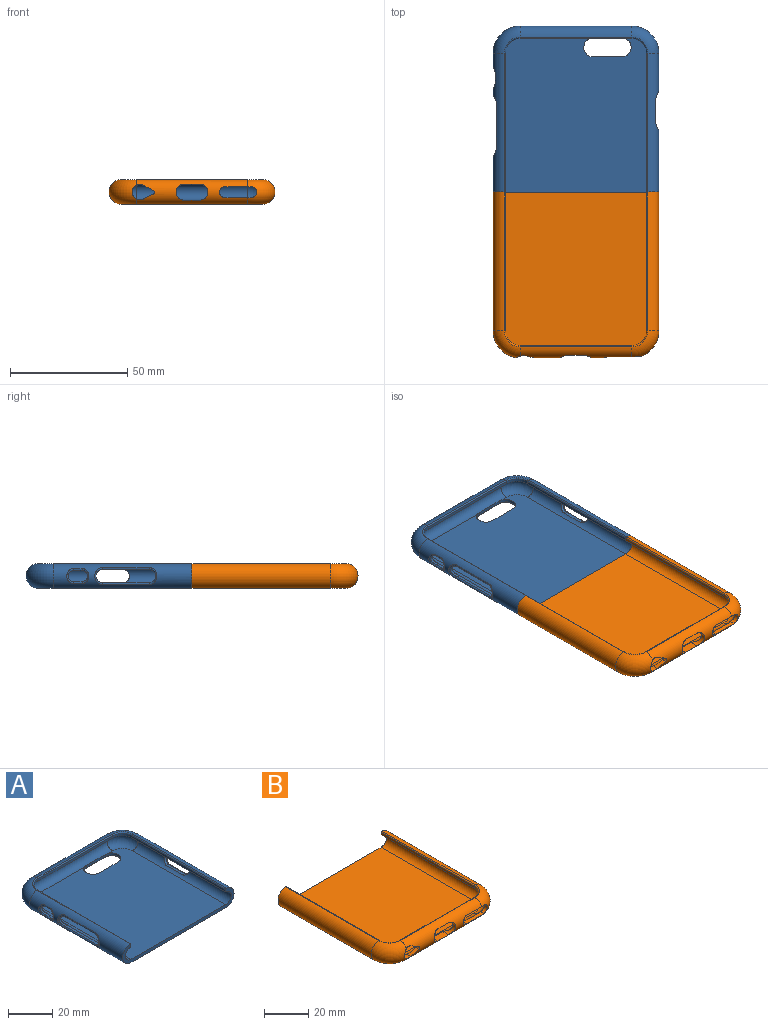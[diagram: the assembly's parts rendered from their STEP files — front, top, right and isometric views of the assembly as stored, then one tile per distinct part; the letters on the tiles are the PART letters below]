
ASSEMBLY  parts=2 mates=1
PART A: 57 faces, bbox 72.7x71.9x10.6 mm
  f0: plane 65.64x60.26mm, normal (0,0,1), area 3790.2mm2, adj f1,f3,f10,f11,f14,f19,f20,f21
  f1: cylinder r=3.5mm len=59.27mm, axis (0,-1,0), area 558.5mm2, adj f0,f2,f11,f40,f41,f42,f43,f56
  f2: plane 59.27x1.24mm, normal (-1,0,0), area 73.7mm2, adj f1,f8,f12,f56
  f3: cylinder r=3.5mm len=59.27mm, axis (0,1,0), area 456.4mm2, adj f0,f4,f14,f32,f33,f34,f35,f36
  f4: plane 59.27x1.24mm, normal (1,0,0), area 73.7mm2, adj f3,f9,f15,f56
  f5: cylinder r=5.28mm len=59.27mm, axis (0,-1,0), area 826.3mm2, adj f7,f8,f16,f44,f45,f46,f47,f56
  f6: cylinder r=5.28mm len=59.27mm, axis (0,1,0), area 691.2mm2, adj f7,f9,f18,f48,f49,f50,f51,f52
  f7: plane 65.64x60.26mm, normal (0,0,-1), area 3772.3mm2, adj f5,f6,f16,f17,f18,f23,f24,f25
  f8: cylinder r=0.51mm len=59.27mm, axis (0,-1,0), area 50.5mm2, adj f2,f5,f29,f56
  f9: cylinder r=0.51mm len=59.27mm, axis (0,1,0), area 50.5mm2, adj f4,f6,f31,f56
  f10: cylinder r=3.5mm len=47.52mm, axis (1,0,0), area 518.9mm2, adj f0,f11,f13,f14,f19,f21,f22
  f11: torus R=6.37mm, axis (0,0,-1), area 148.5mm2, adj f0,f1,f10,f12
  f12: cylinder r=6.37mm len=6.37mm, axis (0,0,-1), area 12.4mm2, adj f2,f11,f13,f29
  f13: plane 47.52x1.24mm, normal (0,-1,0), area 59.1mm2, adj f10,f12,f15,f30
  f14: torus R=6.37mm, axis (0,0,-1), area 148.5mm2, adj f0,f3,f10,f15
  f15: cylinder r=6.37mm len=6.37mm, axis (0,0,-1), area 12.4mm2, adj f4,f13,f14,f31
  f16: torus R=6.37mm, axis (0,0,-1), area 247.6mm2, adj f5,f7,f17,f29
  f17: cylinder r=5.28mm len=47.52mm, axis (1,0,0), area 748mm2, adj f7,f16,f18,f26,f27,f28,f30
  f18: torus R=6.37mm, axis (0,0,-1), area 247.6mm2, adj f6,f7,f17,f31
  f19: cylinder r=4.1mm len=8.2mm, axis (0,0,1), area 16.3mm2, adj f0,f10,f20,f22,f25,f27
  f20: plane 12.06x1.27mm, normal (0,1,0), area 15.3mm2, adj f0,f19,f21,f23
  f21: cylinder r=4.1mm len=8.2mm, axis (0,0,1), area 16.3mm2, adj f0,f10,f20,f22,f24,f26
  f22: plane 12.06x1.22mm, normal (0,-1,0), area 14.7mm2, adj f10,f19,f21,f28
  f23: cylinder r=0.51mm len=12.06mm, axis (1,0,0), area 9.6mm2, adj f7,f20,f24,f25
  f24: torus R=4.61mm, axis (0,0,-1), area 8.7mm2, adj f7,f21,f23,f26
  f25: torus R=4.61mm, axis (0,0,-1), area 8.7mm2, adj f7,f19,f23,f27
  f26: bspline ~4.26x1.79mm, area 2.1mm2, adj f17,f21,f24,f28
  f27: bspline ~4.26x1.79mm, area 2.1mm2, adj f17,f19,f25,f28
  f28: cylinder r=0.51mm len=12.06mm, axis (1,0,0), area 10.6mm2, adj f17,f22,f26,f27
  f29: torus R=6.88mm, axis (0,0,1), area 8.8mm2, adj f8,f12,f16,f30
  f30: cylinder r=0.51mm len=47.52mm, axis (1,0,0), area 40.5mm2, adj f13,f17,f29,f31
  f31: torus R=6.88mm, axis (0,0,1), area 8.8mm2, adj f9,f15,f18,f30
  f32: cylinder r=2.39mm len=4.77mm, axis (1,0,0), area 9.3mm2, adj f3,f33,f35,f55
  f33: plane 3.63x1.22mm, normal (0,0,-1), area 4.4mm2, adj f3,f32,f34,f53
  f34: cylinder r=2.39mm len=4.77mm, axis (1,0,0), area 9.3mm2, adj f3,f33,f35,f52
  f35: plane 3.63x1.24mm, normal (0,0,1), area 4.5mm2, adj f3,f32,f34,f54
  f36: cylinder r=2.8mm len=5.59mm, axis (1,0,0), area 11.3mm2, adj f3,f37,f39,f51
  f37: plane 20.01x1.32mm, normal (0,0,-1), area 26.4mm2, adj f3,f36,f38,f49
  f38: cylinder r=2.8mm len=5.59mm, axis (1,0,0), area 11.3mm2, adj f3,f37,f39,f48
  f39: plane 20.01x1.36mm, normal (0,0,1), area 27.1mm2, adj f3,f36,f38,f50
  f40: plane 10.2x1.32mm, normal (0,0,-1), area 13.4mm2, adj f1,f41,f43,f47
  f41: cylinder r=2.79mm len=5.59mm, axis (-1,0,0), area 11.3mm2, adj f1,f40,f42,f46
  f42: plane 10.2x1.35mm, normal (0,0,1), area 13.8mm2, adj f1,f41,f43,f44
  f43: cylinder r=2.79mm len=5.59mm, axis (-1,0,0), area 11.3mm2, adj f1,f40,f42,f45
  f44: cylinder r=0.51mm len=10.2mm, axis (0,-1,0), area 12.2mm2, adj f5,f42,f45,f46
  f45: bspline ~7.31x3.93mm, area 9.8mm2, adj f5,f43,f44,f47
  f46: bspline ~7.31x3.94mm, area 9.8mm2, adj f5,f41,f44,f47
  f47: cylinder r=0.51mm len=10.2mm, axis (0,-1,0), area 12mm2, adj f5,f40,f45,f46
  f48: bspline ~7.31x3.94mm, area 9.8mm2, adj f6,f38,f49,f50
  f49: cylinder r=0.51mm len=20.01mm, axis (0,1,0), area 23.6mm2, adj f6,f37,f48,f51
  f50: cylinder r=0.51mm len=20.01mm, axis (0,1,0), area 23.9mm2, adj f6,f39,f48,f51
  f51: bspline ~7.31x3.94mm, area 9.8mm2, adj f6,f36,f49,f50
  f52: bspline ~6.41x3.47mm, area 8.2mm2, adj f6,f34,f53,f54
  f53: cylinder r=0.51mm len=3.63mm, axis (0,1,0), area 4.1mm2, adj f6,f33,f52,f55
  f54: cylinder r=0.51mm len=3.63mm, axis (0,1,0), area 4.1mm2, adj f6,f35,f52,f55
  f55: bspline ~6.41x3.48mm, area 8.2mm2, adj f6,f32,f53,f54
  f56: plane 70.82x10.53mm, normal (0,-1,0), area 156mm2, adj f0,f1,f2,f3,f4,f5,f6,f7
PART B: 35 faces, bbox 72.7x71.9x10.5 mm
  f0: plane 47.52x1.24mm, normal (0,1,0), area 59.1mm2, adj f13,f14,f16,f18
  f1: cylinder r=2.32mm len=4.65mm, axis (0,1,0), area 14.2mm2, adj f10,f12,f14,f20
  f2: plane 4.25x3.4mm, normal (-0.43,0,0.9), area 9.7mm2, adj f3,f5,f14,f20
  f3: cylinder r=1mm len=1.92mm, axis (0,1,0), area 4mm2, adj f2,f4,f14,f20
  f4: plane 4.25x3.19mm, normal (-0.43,0,-0.9), area 9.5mm2, adj f3,f5,f14,f20
  f5: cylinder r=3.25mm len=6.5mm, axis (0,1,0), area 30.6mm2, adj f2,f4,f14,f17,f19,f20
  f6: plane 6.85x3.59mm, normal (0,0,1), area 24.6mm2, adj f7,f9,f14,f20
  f7: cylinder r=3.4mm len=6.8mm, axis (0,1,0), area 24.7mm2, adj f6,f8,f14,f20
  f8: plane 6.85x3mm, normal (0,0,-1), area 20.5mm2, adj f7,f9,f14,f20
  f9: cylinder r=3.4mm len=6.8mm, axis (0,1,0), area 24.7mm2, adj f6,f8,f14,f20
  f10: plane 11.25x2.29mm, normal (0,0,1), area 24.3mm2, adj f1,f11,f14,f15,f20,f21
  f11: cylinder r=2.32mm len=4.65mm, axis (0,1,0), area 14.8mm2, adj f10,f12,f15,f21
  f12: plane 11.25x2.23mm, normal (0,0,-1), area 23.5mm2, adj f1,f11,f14,f15,f20,f21
  f13: cylinder r=0.51mm len=47.52mm, axis (-1,0,0), area 40.5mm2, adj f0,f20,f22,f23
  f14: cylinder r=3.5mm len=47.52mm, axis (-1,0,0), area 313.8mm2, adj f0,f1,f2,f3,f4,f5,f6,f7
  f15: torus R=6.37mm, axis (0,0,-1), area 131.1mm2, adj f10,f11,f12,f14,f16,f32,f33
  f16: cylinder r=6.37mm len=6.37mm, axis (0,0,-1), area 12.4mm2, adj f0,f15,f22,f31
  f17: torus R=6.37mm, axis (0,0,-1), area 140.1mm2, adj f5,f14,f18,f30,f33
  f18: cylinder r=6.37mm len=6.37mm, axis (0,0,-1), area 12.4mm2, adj f0,f17,f23,f29
  f19: torus R=6.37mm, axis (0,0,-1), area 239.7mm2, adj f5,f20,f23,f25,f26
  f20: cylinder r=5.28mm len=47.52mm, axis (-1,0,0), area 580mm2, adj f1,f2,f3,f4,f5,f6,f7,f8
  f21: torus R=6.37mm, axis (0,0,-1), area 231.1mm2, adj f10,f11,f12,f20,f22,f25,f28
  f22: torus R=6.88mm, axis (0,0,1), area 8.8mm2, adj f13,f16,f21,f27
  f23: torus R=6.88mm, axis (0,0,1), area 8.8mm2, adj f13,f18,f19,f24
  f24: cylinder r=0.51mm len=59.27mm, axis (0,1,0), area 50.5mm2, adj f23,f26,f29,f34
  f25: plane 65.64x60.26mm, normal (0,0,-1), area 3938.2mm2, adj f19,f20,f21,f26,f28,f34
  f26: cylinder r=5.28mm len=59.27mm, axis (0,1,0), area 949.4mm2, adj f19,f24,f25,f34
  f27: cylinder r=0.51mm len=59.27mm, axis (0,-1,0), area 50.5mm2, adj f22,f28,f31,f34
  f28: cylinder r=5.28mm len=59.27mm, axis (0,-1,0), area 949.4mm2, adj f21,f25,f27,f34
  f29: plane 59.27x1.24mm, normal (1,0,0), area 73.7mm2, adj f18,f24,f30,f34
  f30: cylinder r=3.5mm len=59.27mm, axis (0,1,0), area 651.7mm2, adj f17,f29,f33,f34
  f31: plane 59.27x1.24mm, normal (-1,0,0), area 73.7mm2, adj f16,f27,f32,f34
  f32: cylinder r=3.5mm len=59.27mm, axis (0,-1,0), area 651.7mm2, adj f15,f31,f33,f34
  f33: plane 65.64x60.26mm, normal (0,0,1), area 3938.2mm2, adj f14,f15,f17,f30,f32,f34
  f34: plane 70.82x10.53mm, normal (0,1,0), area 156mm2, adj f24,f25,f26,f27,f28,f29,f30,f31
PLACE A t=(-25.93,10.05,-20.39)mm
PLACE B t=(-25.93,10.05,-20.39)mm
MATE fastened A.f56 <-> B.f34  axis (0,-1,0) through (-25.93,10.05,-20.94)mm
